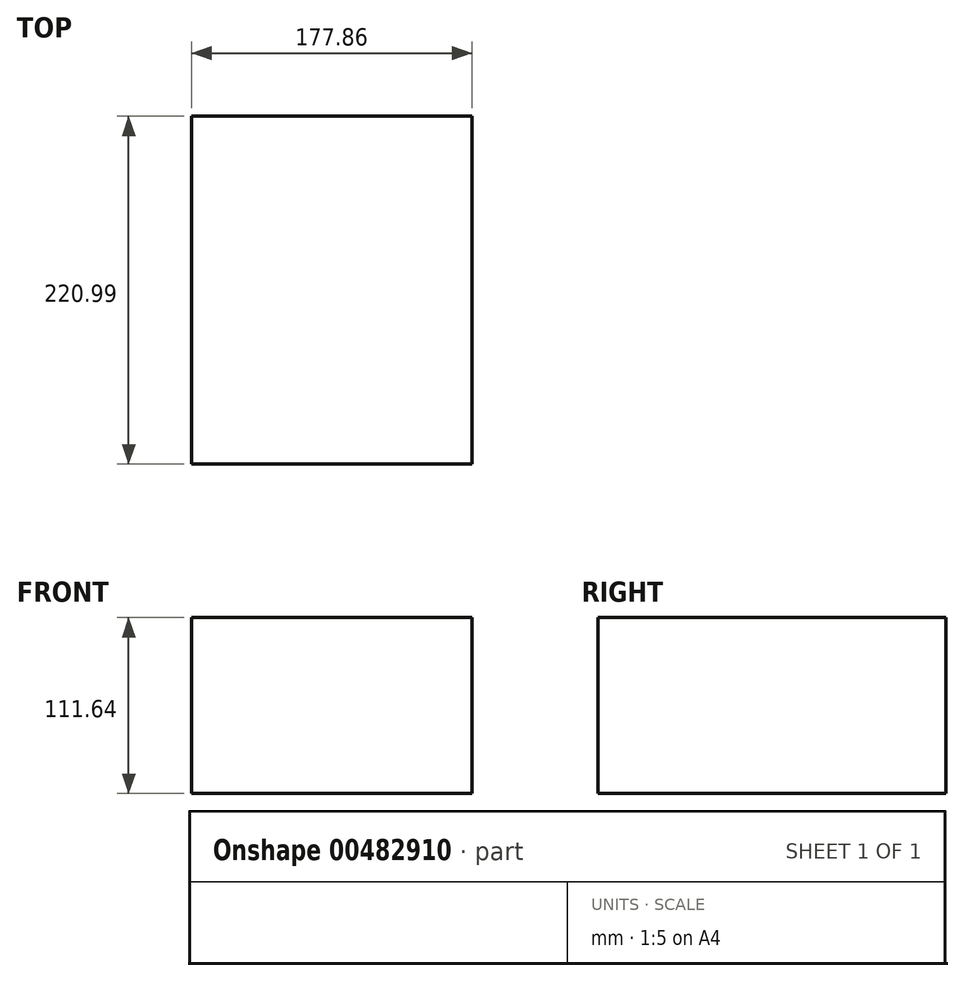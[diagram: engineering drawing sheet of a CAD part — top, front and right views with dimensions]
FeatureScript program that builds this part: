
annotation { "Feature Type Name" : "Feature", "Feature Type Description" : "" }
export const myFeature = defineFeature(function(context is Context, id is Id, definition is map)
    precondition{}
    {
        {
            var Q0;
            Q0=qCreatedBy(makeId("Front.planeOp"),FACE);
            var sketch = newSketch(context, id + "F0", { "sketchPlane" : qUnion([Q0])});
            skLineSegment(sketch, "E0.bottom", {"start": v(-88.93, 55.82) * mm, "end": v(88.93, 55.82) * mm});
            skLineSegment(sketch, "E0.top", {"start": v(-88.93, -55.82) * mm, "end": v(88.93, -55.82) * mm});
            skLineSegment(sketch, "E0.left", {"start": v(-88.93, 55.82) * mm, "end": v(-88.93, -55.82) * mm});
            skLineSegment(sketch, "E0.right", {"start": v(88.93, 55.82) * mm, "end": v(88.93, -55.82) * mm});
            skPoint(sketch, "E0.middle", {"position": v(0, 0) * mm});
            skLineSegment(sketch, "E1.bottom", {"start": v(-50.85, 55.82) * mm, "end": v(-57.64, 55.82) * mm});
            skLineSegment(sketch, "E1.top", {"start": v(-50.85, 55.82) * mm, "end": v(-57.64, 55.82) * mm});
            skLineSegment(sketch, "E1.left", {"start": v(-50.85, 55.82) * mm, "end": v(-50.85, 55.82) * mm});
            skLineSegment(sketch, "E1.right", {"start": v(-57.64, 55.82) * mm, "end": v(-57.64, 55.82) * mm});
            skPoint(sketch, "E1.middle", {"position": v(-54.24, 55.82) * mm});
            skLineSegment(sketch, "E2.bottom", {"start": v(-35.39, 55.82) * mm, "end": v(-66.3, 55.82) * mm});
            skLineSegment(sketch, "E2.top", {"start": v(-35.39, 55.82) * mm, "end": v(-66.3, 55.82) * mm});
            skLineSegment(sketch, "E2.left", {"start": v(-35.39, 55.82) * mm, "end": v(-35.39, 55.82) * mm});
            skLineSegment(sketch, "E2.right", {"start": v(-66.3, 55.82) * mm, "end": v(-66.3, 55.82) * mm});
            skPoint(sketch, "E2.middle", {"position": v(-50.85, 55.82) * mm});
            skSolve(sketch);
        }
        {
            var Q0;
            Q0 = qSketchRegion(id + "F0", true);
            extrude(context, id + "F1", {"entities" : qUnion([Q0]), "depth" : 221 * mm});
        }
    });
